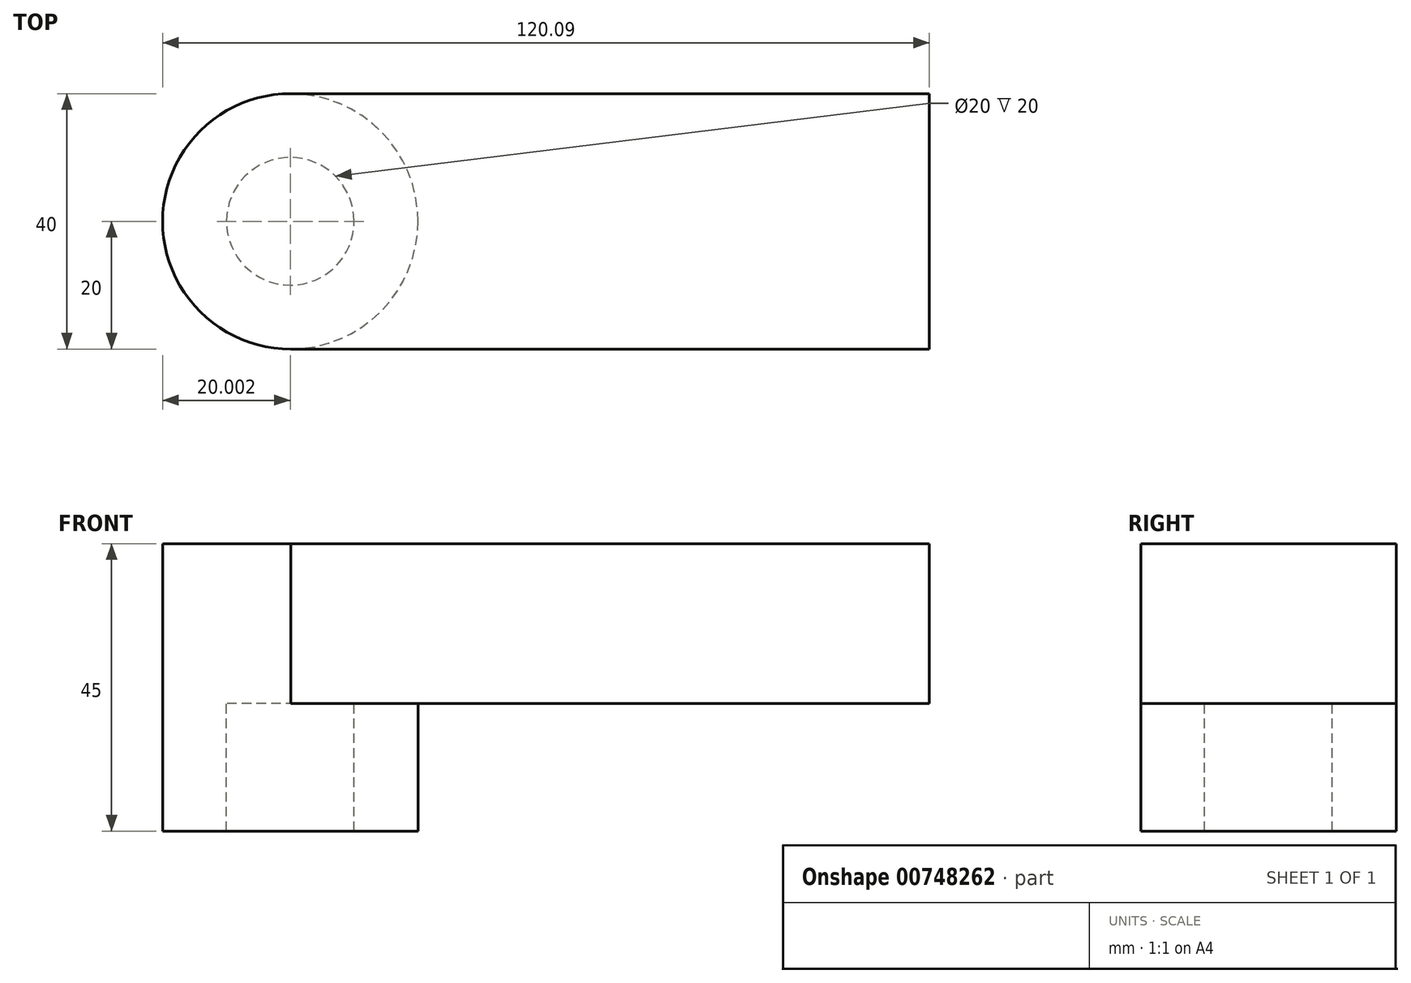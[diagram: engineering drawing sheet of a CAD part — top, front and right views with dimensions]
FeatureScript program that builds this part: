
annotation { "Feature Type Name" : "Feature", "Feature Type Description" : "" }
export const myFeature = defineFeature(function(context is Context, id is Id, definition is map)
    precondition{}
    {
        {
            var Q0;
            Q0=qCreatedBy(makeId("Top.planeOp"),FACE);
            var sketch = newSketch(context, id + "F0", { "sketchPlane" : qUnion([Q0])});
            skCircle(sketch, "E0", {"center": v(-36.63, 20.19) * mm, "radius": 20 * mm});
            skLineSegment(sketch, "E1.bottom", {"start": v(-36.54, 40.19) * mm, "end": v(63.46, 40.19) * mm});
            skLineSegment(sketch, "E1.top", {"start": v(-36.54, 0.19) * mm, "end": v(63.46, 0.19) * mm});
            skLineSegment(sketch, "E1.right", {"start": v(63.46, 40.19) * mm, "end": v(63.46, 0.19) * mm});
            skCircle(sketch, "E2", {"center": v(-36.63, 20.19) * mm, "radius": 10 * mm});
            skLineSegment(sketch, "E3", {"start": v(-36.54, 40.19) * mm, "end": v(-36.54, 0.19) * mm});
            skSolve(sketch);
        }
        {
            var Q0;
            {var subQ0=sQuery(id+"F0.wireOp",EDGE,"E3");var subQ4=sQuery(id+"F0.wireOp",EDGE,"E2");var subQ5=makeQuery(id+"F0.imprint","INTERSECT",VERTEX,{"disambiguationData":[OD(0.0)],"derivedFrom":[subQ4,subQ0]});Q0=makeQuery(id+"F0.imprint","IMPRINT",FACE,{"disambiguationData":[TD([[makeQuery(id+"F0.imprint","IMPRINT",EDGE,{"disambiguationData":[TD([[subQ5,-1.0]])],"derivedFrom":subQ4}),-1.0]])]});}
            var Q1;
            {var subQ0=sQuery(id+"F0.wireOp",EDGE,"E3");var subQ4=sQuery(id+"F0.wireOp",EDGE,"E2");var subQ5=makeQuery(id+"F0.imprint","INTERSECT",VERTEX,{"disambiguationData":[OD(0.0)],"derivedFrom":[subQ4,subQ0]});Q1=makeQuery(id+"F0.imprint","IMPRINT",FACE,{"disambiguationData":[TD([[makeQuery(id+"F0.imprint","IMPRINT",EDGE,{"disambiguationData":[TD([[subQ5,1.0]])],"derivedFrom":subQ4}),-1.0]])]});}
            extrude(context, id + "F1", {"entities" : qUnion([Q0, Q1]), "oppositeDirection" : true, "depth" : 20 * mm, "offsetDistance" : 25 * mm});
        }
        {
            var Q0;
            {var subQ0=sQuery(id+"F0.wireOp",EDGE,"E3");var subQ4=sQuery(id+"F0.wireOp",EDGE,"E2");var subQ5=makeQuery(id+"F0.imprint","INTERSECT",VERTEX,{"disambiguationData":[OD(0.0)],"derivedFrom":[subQ4,subQ0]});Q0=makeQuery(id+"F0.imprint","IMPRINT",FACE,{"disambiguationData":[TD([[makeQuery(id+"F0.imprint","IMPRINT",EDGE,{"disambiguationData":[TD([[subQ5,-1.0]])],"derivedFrom":subQ4}),-1.0]])]});}
            var Q1;
            {var subQ0=sQuery(id+"F0.wireOp",EDGE,"E3");var subQ4=sQuery(id+"F0.wireOp",EDGE,"E2");var subQ5=makeQuery(id+"F0.imprint","INTERSECT",VERTEX,{"disambiguationData":[OD(0.0)],"derivedFrom":[subQ4,subQ0]});Q1=makeQuery(id+"F0.imprint","IMPRINT",FACE,{"disambiguationData":[TD([[makeQuery(id+"F0.imprint","IMPRINT",EDGE,{"disambiguationData":[TD([[subQ5,1.0]])],"derivedFrom":subQ4}),-1.0]])]});}
            var Q2;
            {var subQ0=sQuery(id+"F0.wireOp",EDGE,"E3");var subQ1=sQuery(id+"F0.wireOp",EDGE,"E2");var subQ2=makeQuery(id+"F0.imprint","INTERSECT",VERTEX,{"disambiguationData":[OD(0.0)],"derivedFrom":[subQ1,subQ0]});Q2=makeQuery(id+"F0.imprint","IMPRINT",FACE,{"disambiguationData":[TD([[makeQuery(id+"F0.imprint","IMPRINT",EDGE,{"disambiguationData":[TD([[subQ2,-1.0]])],"derivedFrom":subQ1}),1.0]])]});}
            var Q3;
            {var subQ0=sQuery(id+"F0.wireOp",EDGE,"E3");var subQ1=sQuery(id+"F0.wireOp",EDGE,"E2");var subQ2=makeQuery(id+"F0.imprint","INTERSECT",VERTEX,{"disambiguationData":[OD(0.0)],"derivedFrom":[subQ1,subQ0]});Q3=makeQuery(id+"F0.imprint","IMPRINT",FACE,{"disambiguationData":[TD([[makeQuery(id+"F0.imprint","IMPRINT",EDGE,{"disambiguationData":[TD([[subQ2,1.0]])],"derivedFrom":subQ1}),1.0]])]});}
            var Q4;
            {var subQ1=sQuery(id+"F0.wireOp",EDGE,"E1.bottom");Q4=makeQuery(id+"F0.imprint","IMPRINT",FACE,{"disambiguationData":[TD([[makeQuery(id+"F0.imprint","IMPRINT",EDGE,{"derivedFrom":subQ1}),-1.0]])]});}
            extrude(context, id + "F2", {"entities" : qUnion([Q0, Q1, Q2, Q3, Q4]), "operationType" : NewBodyOperationType.ADD, "depth" : 25 * mm, "offsetDistance" : 25 * mm});
        }
    });
